# Revit family: 2025.04.28 - ME862 REVIT
name_source: partatom
category: Generic Models
revit_build: Autodesk Revit 2018 (Build: 20180423_1000(x64)
units: mm (PartAtom-declared; Revit-internal decimal feet)

## family parameters
Always vertical = Yes
Can host rebar = No
Cut with Voids When Loaded = No
Part Type = Normal
Room Calculation Point = No
Round Connector Dimension = Use Diameter
Shared = No
Work Plane-Based = No

## types (1)
- 2025.04.28 - ME862 REVIT
    CONNECTIVITY - Input Terminals - Data = USB 3.0 x1 (5V/0/9A, Downstream), USB 2.0 x1 (5V/0.5A, Downstream), USB 3.0 (Downstream for USB-C), USB-C x1 (Upstream)
    CONNECTIVITY - Input Terminals - Digital = HDMI 2.0 x3, USB-C x1 (DP-Alt Mode Supported)
    CONNECTIVITY - Input Terminals - External Control = LAN (1000Mbit), 3.5mm Mini Jack IR Remote, RS-232C
    CONNECTIVITY - Output Terminals - Audio = 3.5mm Mini Jack, Optical Audio Out (SPDIF)
    ENVIRONMENTAL CONDITIONS - Operating Altitude = 5,000m(16,405ft)
    ENVIRONMENTAL CONDITIONS - Operating Humidity = 20-80%
    ENVIRONMENTAL CONDITIONS - Operating Temperature = 0° - 40° C/ 32 - 104° F
    INTERNAL PLAYER - Memory = 4GB
    INTERNAL PLAYER - Operating System = Android 13
    INTERNAL PLAYER - Processor = ARM Cortex-A55 1.5GHz Quad Core CPU
    INTERNAL PLAYER - Storage = 32GB ROM (Total Capacity of Storage including OS)
    LCD MODULE - Aspect Ration = 16:9
    LCD MODULE - Brightness (Typical) = 450 cd/m2
    LCD MODULE - Color Gamut = 72% NTSC
    LCD MODULE - Contrast Ratio (Typical) = 1200:1
    LCD MODULE - Displayable Colors = Over 1.07 Billion (8 bit + FRC)
    LCD MODULE - Native Resolution = 3840x2160
    LCD MODULE - Orientation = Landscape and Portrait (CW Rotation)
    LCD MODULE - Panel Haze (%) = 25 (Anti-Reflective)
    LCD MODULE - Panel Technology = ADS
    LCD MODULE - Viewable Image Size = 85.6"
    LCD MODULE - Viewing Angle = 178° Vert., 178° Hor. (89U/89D/89L/89R) @ CR>10
    LIMITED WARRANTY = 3 years Advanced Replacement
    Manufacturer = NEC Display Solutions
    Model = ME862
    OPTIONAL SPEAKERS = SP-RM3a
    OPTIONAL STAND = ST-801
    OTHER ACCESSORIES = Wifi6 Module (S107B), Human Sensor (KT-RC3)
    PHYSICAL SPECIFICATIONS - Bezel Width (L/R, T/B) = 15.9mm/15.9mm/15.9mm/15.9mm
    PHYSICAL SPECIFICATIONS - Net Dimensions (Without stand - W x H x D) = 76.0 x 43.4 x 2.7 in. (1930.8 x 1101.7 x 68.0mm)
    PHYSICAL SPECIFICATIONS - Net Weight = 42.0kg / 92.6lbs.
    PHYSICAL SPECIFICATIONS - VESA Hole Configuration = 4x M8 x 18mm (800 x 600)
    POWER CONSUMPTION - Current Rating = 4.1 - 1.9A @100V - 240V
    POWER CONSUMPTION - Network Standby = 2W
    POWER CONSUMPTION - Normal Standby = <0.5W
    POWER CONSUMPTION - On (Typ/Max Brightness/All Max = 162W/295W/405W
    POWER CONSUMPTION - Speaker Rating = Integrated 10W x 10W, Optional through SP-RM3a
    SENSORS - Ambient Light Sensor = Integrated
    SENSORS - Human Sensor = Optional (KT-RC3)
    SENSORS - Temperature Sensor = Integrated
    SHIPS WITH = 3m AC Power Cord, 2.0mm HDMI Cable, IR Remote Control, Batteries, AAA batteries
    URL = www.necdisplay.com

## geometry (parser evidence)
native form markers: Sweep x11
no freeform markers — native parametric forms only
